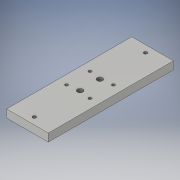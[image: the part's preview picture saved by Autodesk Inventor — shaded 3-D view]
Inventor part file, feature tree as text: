
AUTODESK INVENTOR PART (.ipt)
format: ipt  version: 2019.4 (Build 234330000, 330)  size: 146,432 bytes
history: native  units: in
note: dims shown in document units (in); Inventor stores cm internally (conversion verified against a paired STEP export)
features: sketch x4, hole x3, extrude x1, chamfer x1
ambient origin geometry x8: Origin, YZ Plane, XZ Plane, XY Plane, X Axis, Y Axis, Z Axis, Center Point
bodies: Solid1 (feature_tree)
feature tree (9):
  extrude  "Extrusion1"  Depth=1.181in
  hole  "Hole2"  [1 undecoded]
  hole  "Hole3"  [1 undecoded]
  chamfer  "Chamfer2"  Distance=0.163in
  sketch  "Sketch1"  dims[d0=3.543in d1=1.181in]
  sketch  "Sketch5"  dims[d2=0.25in d3=0.0in d33=0.118in]
  sketch  "Sketch6"  dims[d34=0.118in d35=0.197in]
  sketch  "Sketch7"  dims[d36=0.197in d37=0.097in d38=0.2in d39=0.375in d40=0.25in d41=0.5635in d42=0.22in d43=0.8108in d44=0.163in d45=0.2795in d46=0.163in d47=0.2795in d48=0.156in d49=0.38in d50=0.375in d51=0.25in d52=0.5635in d53=0.536in d54=0.8108in d55=0.18in d56=0.663in d57=0.663in d59=0.7874in d61=0.7874in d62=0.118in d63=0.3315in d64=0.3315in d65=0.8108in d66=0.5635in d67=0.25in d68=0.375in d69=0.22in d70=0.085in d71=0.028in d72=0.125in d73=45.0deg]
  hole  "Hole4"  [1 undecoded]
note: 3 required parameter values undecoded (feature->parameter linkage not recoverable at this tier; creation-order binding heuristic only, values carry confidence <= 0.55)
